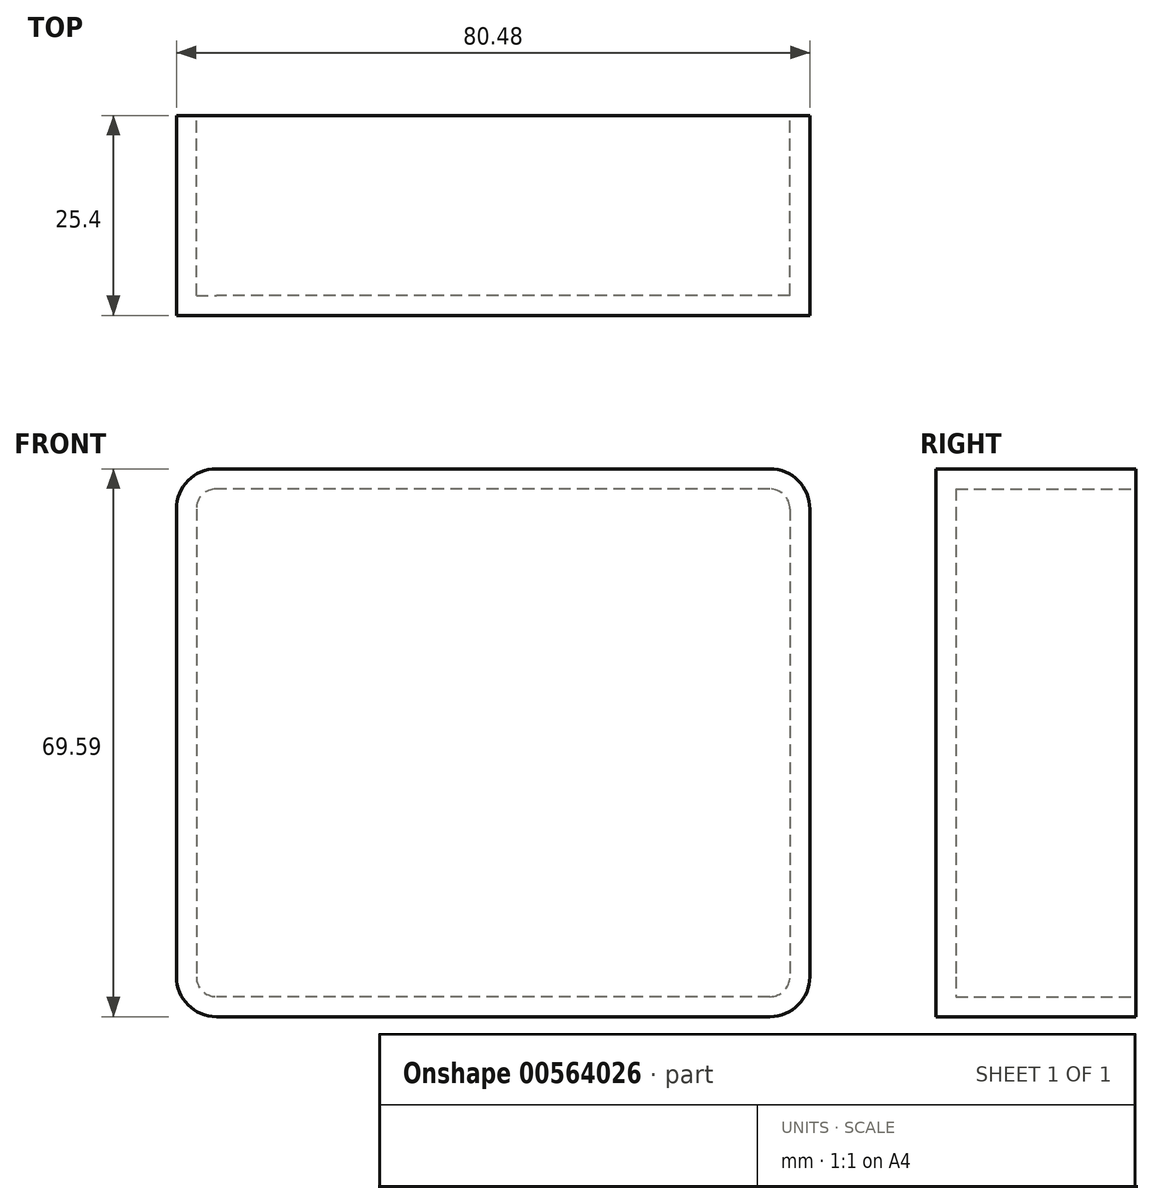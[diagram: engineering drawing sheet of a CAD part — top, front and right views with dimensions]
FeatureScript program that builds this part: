
annotation { "Feature Type Name" : "Feature", "Feature Type Description" : "" }
export const myFeature = defineFeature(function(context is Context, id is Id, definition is map)
    precondition{}
    {
        {
            var Q0;
            Q0=qCreatedBy(makeId("Front.planeOp"),FACE);
            var sketch = newSketch(context, id + "F0", { "sketchPlane" : qUnion([Q0])});
            skLineSegment(sketch, "E0.bottom", {"start": v(14.26, 52.1) * mm, "end": v(-66.22, 52.1) * mm});
            skLineSegment(sketch, "E0.top", {"start": v(14.26, -17.48) * mm, "end": v(-66.22, -17.48) * mm});
            skLineSegment(sketch, "E0.left", {"start": v(14.26, 52.1) * mm, "end": v(14.26, -17.48) * mm});
            skLineSegment(sketch, "E0.right", {"start": v(-66.22, 52.1) * mm, "end": v(-66.22, -17.48) * mm});
            skSolve(sketch);
        }
        {
            var Q0;
            Q0=makeQuery(id+"F0.imprint","IMPRINT",FACE,{"disambiguationData":[TD([[makeQuery(id+"F0.imprint","IMPRINT",EDGE,{"derivedFrom":sQuery(id+"F0.wireOp",EDGE,"E0.bottom")}),1.0]])]});
            extrude(context, id + "F1", {"entities" : qUnion([Q0]), "depth" : 25.4 * mm, "offsetDistance" : 25.4 * mm});
        }
        {
            var Q0;
            Q0=makeQuery(id+"F1.opExtrude","SWEPT_EDGE",EDGE,{"disambiguationData":[OSD([sQuery(id+"F0.wireOp",EDGE,"E0.bottom"),sQuery(id+"F0.wireOp",EDGE,"E0.left")])]});
            var Q1;
            Q1=makeQuery(id+"F1.opExtrude","SWEPT_EDGE",EDGE,{"disambiguationData":[OSD([sQuery(id+"F0.wireOp",EDGE,"E0.bottom"),sQuery(id+"F0.wireOp",EDGE,"E0.right")])]});
            var Q2;
            Q2=makeQuery(id+"F1.opExtrude","SWEPT_EDGE",EDGE,{"disambiguationData":[OSD([sQuery(id+"F0.wireOp",EDGE,"E0.top"),sQuery(id+"F0.wireOp",EDGE,"E0.right")])]});
            var Q3;
            Q3=makeQuery(id+"F1.opExtrude","SWEPT_EDGE",EDGE,{"disambiguationData":[OSD([sQuery(id+"F0.wireOp",EDGE,"E0.top"),sQuery(id+"F0.wireOp",EDGE,"E0.left")])]});
            fillet(context, id + "F2", {"entities" : qUnion([Q0, Q1, Q2, Q3]), "radius" : 5.08 * mm, "tangentPropagation" : true, "allowEdgeOverflow" : false});
        }
        {
            var Q0;
            Q0=makeQuery(id+"F1.opExtrude","CAP_FACE",FACE,{"disambiguationData":[OSD([sQuery(id+"F0.wireOp",EDGE,"E0.bottom"),sQuery(id+"F0.wireOp",EDGE,"E0.top"),sQuery(id+"F0.wireOp",EDGE,"E0.left"),sQuery(id+"F0.wireOp",EDGE,"E0.right")])],"isStart":true});
            shell(context, id + "F3", {"entities" : qUnion([Q0]), "thickness" : 2.54 * mm});
        }
    });
